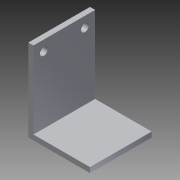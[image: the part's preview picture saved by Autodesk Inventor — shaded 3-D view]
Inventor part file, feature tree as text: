
AUTODESK INVENTOR PART (.ipt)
format: ipt  version: 2013 (Build 170138000, 138)  size: 87,040 bytes
history: native  units: in
note: dims shown in document units (in); Inventor stores cm internally (conversion verified against a paired STEP export)
features: extrude x2, sketch x2
ambient origin geometry x8: Origin, YZ Plane, XZ Plane, XY Plane, X Axis, Y Axis, Z Axis, Center Point
bodies: Solid1 (feature_tree)
feature tree (4):
  extrude  "Extrusion1"  Depth=2.0in
  extrude  "Extrusion2"  Depth=1.5in TaperAngle=0.0deg
  sketch  "Sketch1"  dims[d0=1.5in d1=2.0in]
  sketch  "Sketch2"  dims[d2=0.125in d3=1.5in d4=0.0in d5=1.0in d6=0.25in d7=0.1875in d8=0.1875in d9=1.5in d10=0.0in]
